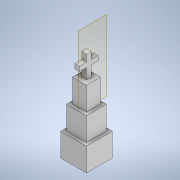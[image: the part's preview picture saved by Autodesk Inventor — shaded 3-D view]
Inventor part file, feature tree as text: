
AUTODESK INVENTOR PART (.ipt)
format: ipt  version: 2021 (Build 250183000, 183)  size: 150,528 bytes
history: native  units: in
note: dims shown in document units (in); Inventor stores cm internally (conversion verified against a paired STEP export)
features: extrude x4, sketch x4, plane x1
ambient origin geometry x8: Origin, YZ Plane, XZ Plane, XY Plane, X Axis, Y Axis, Z Axis, Center Point
bodies: Solid1 (feature_tree)
feature tree (9):
  extrude  "Extrusion1"  Depth=0.4724in
  plane  "Work Plane1"
  extrude  "Extrusion2"  Depth=0.0787in
  extrude  "Extrusion3"  Depth=0.2362in
  extrude  "Extrusion4"  Depth=0.2362in
  sketch  "Sketch1"  dims[d0=0.4724in d1=0.4724in]
  sketch  "Sketch2"  dims[d2=0.7874in d3=0.0in d4=0.0787in]
  sketch  "Sketch3"  dims[d5=0.3543in d6=0.2362in]
  sketch  "Sketch4"  dims[d7=0.1575in d8=0.2362in d9=0.1575in d10=0.2362in d11=0.1575in d12=0.0in d15=0.0984in d16=0.0984in d17=0.6693in d18=0.6693in d19=0.7874in d20=0.0in d21=0.0984in d22=0.0984in d23=0.8661in d24=0.8661in d25=0.7874in d26=0.0in]
